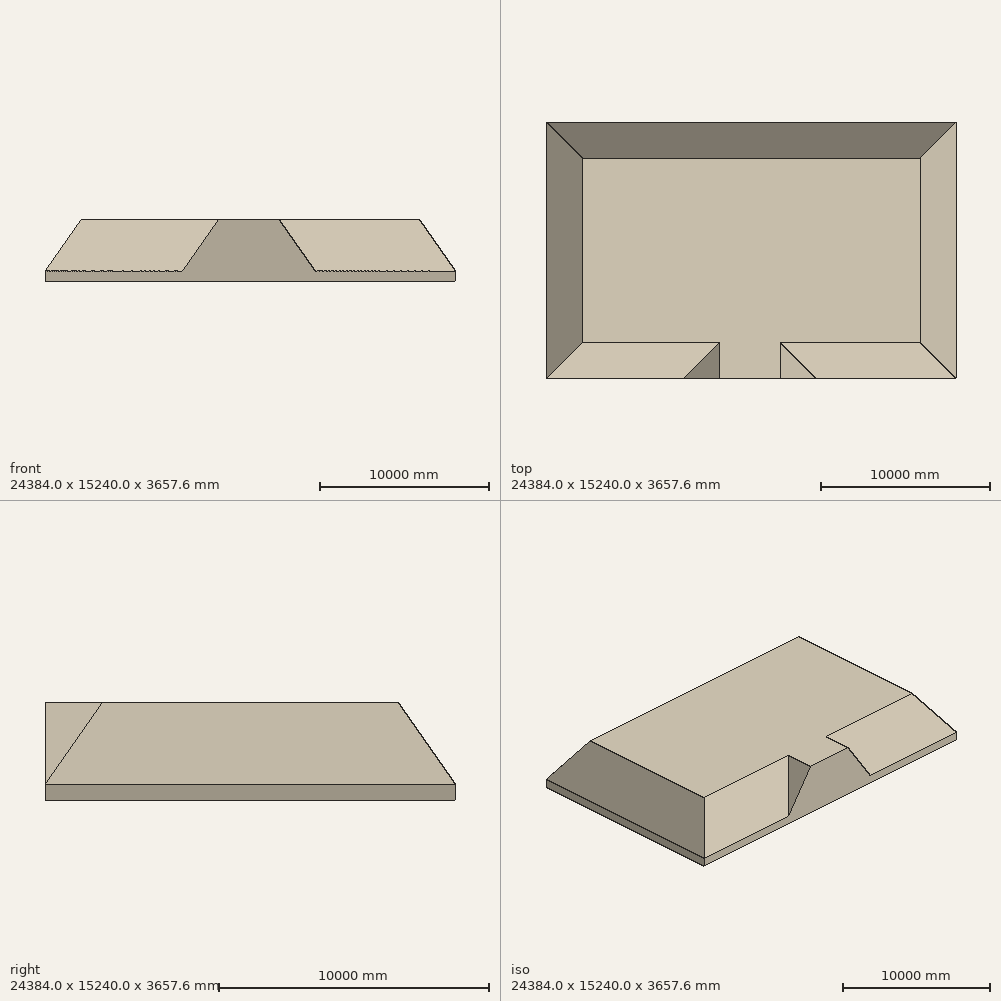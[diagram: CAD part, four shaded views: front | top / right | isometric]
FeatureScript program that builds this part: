
annotation { "Feature Type Name" : "Feature", "Feature Type Description" : "" }
export const myFeature = defineFeature(function(context is Context, id is Id, definition is map)
    precondition{}
    {
        {
            var Q0;
            Q0=qCreatedBy(makeId("Top.planeOp"),FACE);
            var sketch = newSketch(context, id + "F0", { "sketchPlane" : qUnion([Q0])});
            skLineSegment(sketch, "E0.bottom", {"start": v(0, 0) * mm, "end": v(24384, 0) * mm});
            skLineSegment(sketch, "E0.top", {"start": v(0, 15240) * mm, "end": v(24384, 15240) * mm});
            skLineSegment(sketch, "E0.left", {"start": v(0, 0) * mm, "end": v(0, 15240) * mm});
            skLineSegment(sketch, "E0.right", {"start": v(24384, 0) * mm, "end": v(24384, 15240) * mm});
            skSolve(sketch);
        }
        {
            var Q0;
            Q0 = qSketchRegion(id + "F0", true);
            extrude(context, id + "F1", {"entities" : qUnion([Q0]), "depth" : 3657.6 * mm});
        }
        {
            var Q0;
            Q0=makeQuery(id+"F1.opExtrude","CAP_EDGE",EDGE,{"disambiguationData":[OSD([sQuery(id+"F0.wireOp",EDGE,"E0.bottom")])],"isStart":false});
            var Q1;
            Q1=makeQuery(id+"F1.opExtrude","CAP_EDGE",EDGE,{"disambiguationData":[OSD([sQuery(id+"F0.wireOp",EDGE,"E0.left")])],"isStart":false});
            var Q2;
            Q2=makeQuery(id+"F1.opExtrude","CAP_EDGE",EDGE,{"disambiguationData":[OSD([sQuery(id+"F0.wireOp",EDGE,"E0.top")])],"isStart":false});
            var Q3;
            Q3=makeQuery(id+"F1.opExtrude","CAP_EDGE",EDGE,{"disambiguationData":[OSD([sQuery(id+"F0.wireOp",EDGE,"E0.right")])],"isStart":false});
            chamfer(context, id + "F2", {"entities" : qUnion([Q0, Q1, Q2, Q3]), "chamferType" : ChamferType.OFFSET_ANGLE, "width" : 3048 * mm, "oppositeDirection" : true, "angle" : 35 * degree, "tangentPropagation" : true});
        }
        {
            var Q0;
            Q0=makeQuery(id+"F1.opExtrude","SWEPT_FACE",FACE,{"disambiguationData":[OSD([sQuery(id+"F0.wireOp",EDGE,"E0.bottom")])]});
            var sketch = newSketch(context, id + "F3", { "sketchPlane" : qUnion([Q0])});
            skLineSegment(sketch, "E1.0", {"start": v(10305.08, 3657.6) * mm, "end": v(13905.62, 3657.6) * mm});
            skLineSegment(sketch, "E2.0", {"start": v(8170.85, 0) * mm, "end": v(16039.85, 0) * mm});
            skLineSegment(sketch, "E3", {"start": v(12192, 3657.6) * mm, "end": v(12192, 6484.87) * mm, "construction": true});
            skLineSegment(sketch, "E4", {"start": v(10305.08, 3657.6) * mm, "end": v(8170.85, 609.6) * mm});
            skLineSegment(sketch, "E5", {"start": v(8170.85, 609.6) * mm, "end": v(8170.85, 0) * mm});
            skLineSegment(sketch, "E6", {"start": v(13905.62, 3657.6) * mm, "end": v(16039.85, 609.6) * mm});
            skLineSegment(sketch, "E7", {"start": v(16039.85, 609.6) * mm, "end": v(16039.85, 0) * mm});
            skPoint(sketch, "E8.orphan", {"position": v(2134.23, 3657.6) * mm});
            skPoint(sketch, "E9.orphan", {"position": v(0, 0) * mm});
            skPoint(sketch, "E10.orphan", {"position": v(24384, 0) * mm});
            skPoint(sketch, "E11.orphan", {"position": v(22249.77, 3657.6) * mm});
            skSolve(sketch);
        }
        {
            var Q0;
            Q0 = qSketchRegion(id + "F3", true);
            var Q1;
            Q1=makeQuery(id+"F2.opChamfer","BLEND_FACE",FACE,{"disambiguationData":[OSD([sQuery(id+"F0.wireOp",EDGE,"E0.bottom")])]});
            extrude(context, id + "F4", {"entities" : qUnion([Q0]), "operationType" : NewBodyOperationType.ADD, "endBound" : BoundingType.UP_TO_SURFACE, "oppositeDirection" : true, "endBoundEntityFace" : qUnion([Q1]), "depth" : 2779.08 * mm});
        }
        {
            var Q0;
            Q0=makeQuery(id+"F1.opExtrude","CAP_FACE",FACE,{"disambiguationData":[OSD([sQuery(id+"F0.wireOp",EDGE,"E0.bottom"),sQuery(id+"F0.wireOp",EDGE,"E0.top"),sQuery(id+"F0.wireOp",EDGE,"E0.left"),sQuery(id+"F0.wireOp",EDGE,"E0.right")])],"isStart":true});
            shell(context, id + "F5", {"entities" : qUnion([Q0]), "thickness" : 152.4 * mm});
        }
    });
